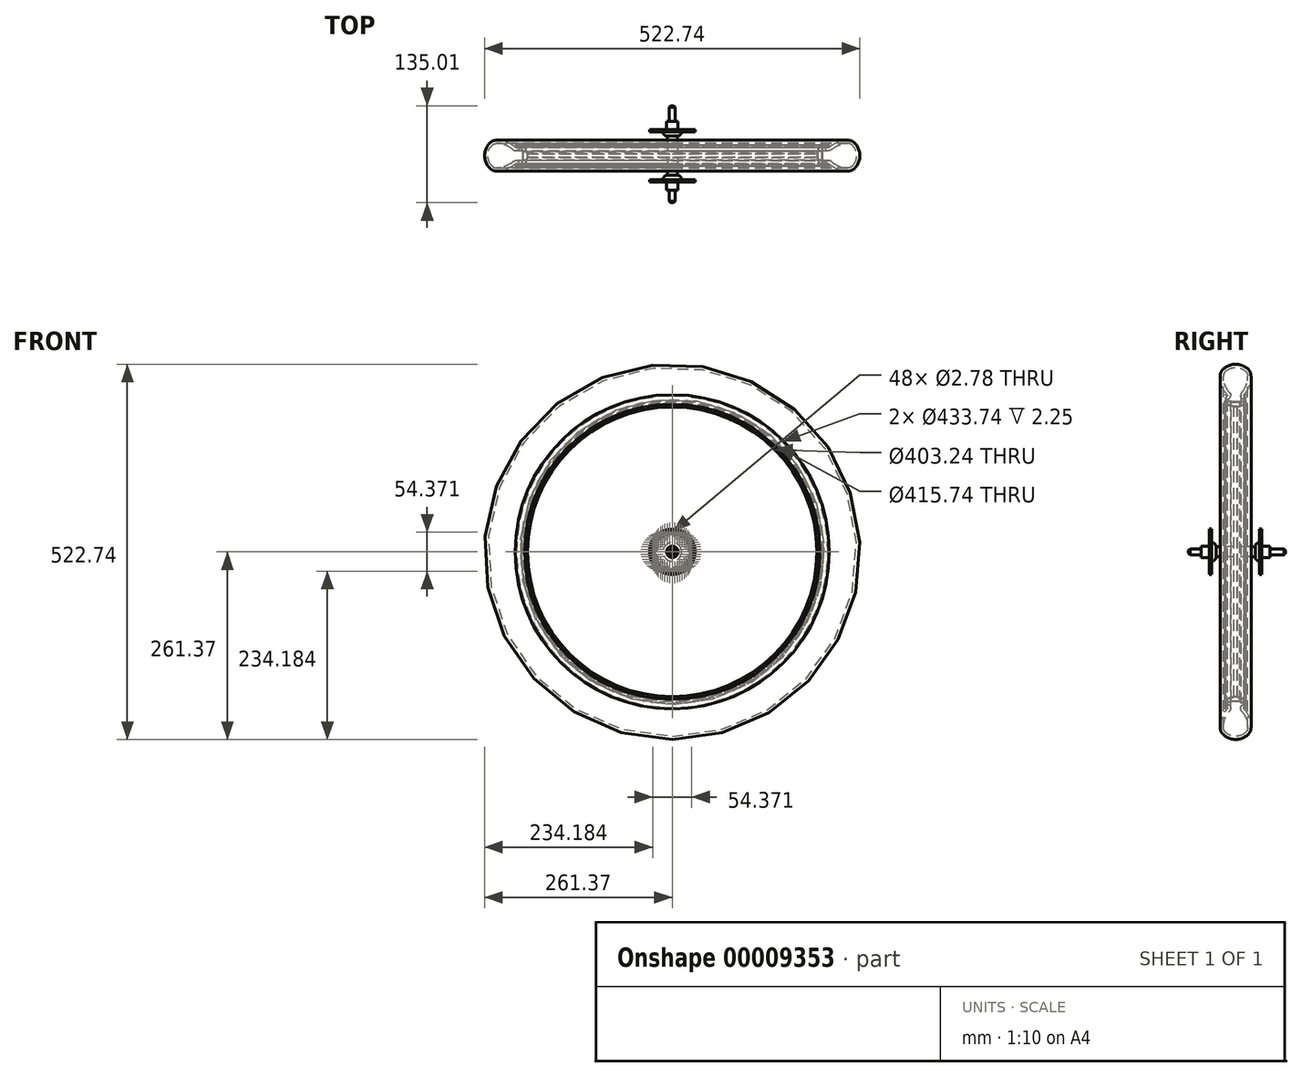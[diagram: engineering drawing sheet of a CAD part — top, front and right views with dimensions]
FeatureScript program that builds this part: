
annotation { "Feature Type Name" : "Feature", "Feature Type Description" : "" }
export const myFeature = defineFeature(function(context is Context, id is Id, definition is map)
    precondition{}
    {
        {
            var Q0;
            Q0=qCreatedBy(makeId("Front.planeOp"),FACE);
            var sketch = newSketch(context, id + "F0", { "sketchPlane" : qUnion([Q0])});
            skCircle(sketch, "E0", {"center": v(0, 0) * mm, "radius": 31.75 * mm});
            skCircle(sketch, "E1", {"center": v(0, 0) * mm, "radius": 4 * mm});
            skSolve(sketch);
        }
        {
            var Q0;
            Q0=qSketchRegion(id+"F0",true);
            extrude(context, id + "F1", {"entities" : qUnion([Q0]), "depth" : 3.17 * mm});
        }
        {
            var Q0;
            Q0=qCreatedBy(makeId("Right.planeOp"),FACE);
            var sketch = newSketch(context, id + "F2", { "sketchPlane" : qUnion([Q0])});
            skLineSegment(sketch, "E2", {"start": v(-31.75, 0) * mm, "end": v(31.75, 0) * mm, "construction": true});
            skLineSegment(sketch, "E3", {"start": v(-31.75, 27.19) * mm, "end": v(31.75, 27.19) * mm, "construction": true});
            skPoint(sketch, "E4", {"position": v(-3.18, 28.57) * mm});
            skLineSegment(sketch, "E5", {"start": v(-3.18, 31.75) * mm, "end": v(0, 31.75) * mm, "construction": true});
            skSolve(sketch);
        }
        {
            var Q0;
            Q0=qCreatedBy(makeId("Right.planeOp"),FACE);
            var sketch = newSketch(context, id + "F3", { "sketchPlane" : qUnion([Q0])});
            skLineSegment(sketch, "E6", {"start": v(-3.18, 27.19) * mm, "end": v(-3.18, 29.37) * mm});
            skLineSegment(sketch, "E7", {"start": v(-3.18, 29.37) * mm, "end": v(-2.7, 28.57) * mm});
            skLineSegment(sketch, "E8", {"start": v(-2.7, 28.57) * mm, "end": v(-0.48, 28.57) * mm});
            skLineSegment(sketch, "E9", {"start": v(-0.48, 28.57) * mm, "end": v(0, 29.37) * mm});
            skLineSegment(sketch, "E10", {"start": v(0, 29.37) * mm, "end": v(0, 27.19) * mm});
            skLineSegment(sketch, "E11", {"start": v(0, 27.19) * mm, "end": v(-3.18, 27.19) * mm});
            skLineSegment(sketch, "E12", {"start": v(-1.59, 27.19) * mm, "end": v(-1.59, 31.75) * mm, "construction": true});
            skSolve(sketch);
        }
        {
            var Q0;
            Q0=qSketchRegion(id+"F3",true);
            var Q1;
            Q1=sQuery(id+"F2.wireOp",EDGE,"E3");
            revolve(context, id + "F4", {"entities" : qUnion([Q0]), "axis" : qUnion([Q1]), "revolveType" : RevolveType.FULL, "oppositeDirection" : true});
        }
        {
            var Q0;
            Q0=makeQuery(id+"F4.opRevolve","SWEPT_BODY",BODY,{"disambiguationData":[OSD([sQuery(id+"F3.wireOp",EDGE,"E6"),sQuery(id+"F3.wireOp",EDGE,"E7"),sQuery(id+"F3.wireOp",EDGE,"E8"),sQuery(id+"F3.wireOp",EDGE,"E9"),sQuery(id+"F3.wireOp",EDGE,"E10"),sQuery(id+"F3.wireOp",EDGE,"E11")])]});
            var Q1;
            Q1=sQuery(id+"F2.wireOp",EDGE,"E2");
            circularPattern(context, id + "F5", {"operationType" : NewBodyOperationType.REMOVE, "entities" : qUnion([Q0]), "axis" : qUnion([Q1]), "angle" : 360 * degree, "instanceCount" : round(24), "equalSpace" : true});
        }
        {
            var Q0;
            Q0=makeQuery(id+"F1.opExtrude","SWEPT_BODY",BODY,{"disambiguationData":[OSD([sQuery(id+"F0.wireOp",EDGE,"E0"),sQuery(id+"F0.wireOp",EDGE,"E1")])]});
            var Q1;
            Q1=sQuery(id+"F2.wireOp",EDGE,"E2");
            transform(context, id + "F6", {"entities" : qUnion([Q0]), "transformType" : TransformType.TRANSLATION_DISTANCE, "transformDirection" : qUnion([Q1]), "distance" : 69.85 * mm, "makeCopy" : true});
        }
        {
            var Q0;
            Q0=makeQuery(id+"F6.opPattern","COPY",BODY,{"derivedFrom":makeQuery(id+"F1.opExtrude","SWEPT_BODY",BODY,{"disambiguationData":[OSD([sQuery(id+"F0.wireOp",EDGE,"E0"),sQuery(id+"F0.wireOp",EDGE,"E1")])]}),"instanceName":"1"});
            var Q1;
            Q1=sQuery(id+"F2.wireOp",EDGE,"E2");
            transform(context, id + "F7", {"entities" : qUnion([Q0]), "transformType" : TransformType.ROTATION, "transformAxis" : qUnion([Q1]), "angle" : 7.5 * degree, "makeCopy" : false});
        }
        {
            var Q0;
            Q0=qCreatedBy(makeId("Right.planeOp"),FACE);
            var sketch = newSketch(context, id + "F8", { "sketchPlane" : qUnion([Q0])});
            skLineSegment(sketch, "E13", {"start": v(0, 0) * mm, "end": v(66.68, 0) * mm, "construction": true});
            skLineSegment(sketch, "E14", {"start": v(33.34, 0) * mm, "end": v(33.34, 218.87) * mm, "construction": true});
            skSolve(sketch);
        }
        {
            var Q0;
            Q0=qCreatedBy(makeId("Front.planeOp"),FACE);
            var Q1;
            Q1=sQuery(id+"F8.wireOp",VERTEX,"E14.start");
            cPlane(context, id + "F9", {"entities" : qUnion([Q0, Q1]), "cplaneType" : CPlaneType.PLANE_POINT, "offset" : 150 * mm, "width" : 150 * mm, "height" : 150 * mm});
        }
        {
            var Q0;
            Q0=qCreatedBy(id+"F9.planeOp",FACE);
            var sketch = newSketch(context, id + "F10", { "sketchPlane" : qUnion([Q0])});
            skCircle(sketch, "E15", {"center": v(0, 0) * mm, "radius": 218.87 * mm, "construction": true});
            skSolve(sketch);
        }
        {
            var Q0;
            Q0=qCreatedBy(makeId("Right.planeOp"),FACE);
            var sketch = newSketch(context, id + "F11", { "sketchPlane" : qUnion([Q0])});
            skLineSegment(sketch, "E16", {"start": v(33.34, 201.62) * mm, "end": v(30.84, 201.62) * mm});
            skLineSegment(sketch, "E17", {"start": v(18.34, 218.87) * mm, "end": v(21.59, 218.87) * mm});
            skLineSegment(sketch, "E18", {"start": v(18.34, 218.87) * mm, "end": v(18.34, 205.53) * mm});
            skLineSegment(sketch, "E19", {"start": v(18.34, 205.53) * mm, "end": v(30.84, 201.62) * mm});
            skLineSegment(sketch, "E20", {"start": v(21.59, 218.87) * mm, "end": v(21.59, 216.87) * mm});
            skLineSegment(sketch, "E21", {"start": v(21.59, 216.87) * mm, "end": v(19.34, 216.87) * mm});
            skLineSegment(sketch, "E22", {"start": v(19.34, 216.87) * mm, "end": v(19.34, 211.37) * mm});
            skLineSegment(sketch, "E23", {"start": v(19.34, 211.37) * mm, "end": v(27.34, 208.87) * mm});
            skLineSegment(sketch, "E24", {"start": v(27.34, 208.87) * mm, "end": v(33.34, 208.87) * mm});
            skLineSegment(sketch, "E25", {"start": v(33.34, 207.87) * mm, "end": v(27.18, 207.87) * mm});
            skLineSegment(sketch, "E26", {"start": v(27.18, 207.87) * mm, "end": v(19.34, 210.32) * mm});
            skLineSegment(sketch, "E27", {"start": v(19.34, 210.32) * mm, "end": v(19.34, 206.26) * mm});
            skLineSegment(sketch, "E28", {"start": v(19.34, 206.26) * mm, "end": v(31, 202.62) * mm});
            skLineSegment(sketch, "E29", {"start": v(31, 202.62) * mm, "end": v(33.34, 202.62) * mm});
            skLineSegment(sketch, "E30", {"start": v(19.34, 214.12) * mm, "end": v(18.34, 214.12) * mm, "construction": true});
            skLineSegment(sketch, "E31", {"start": v(23.34, 210.12) * mm, "end": v(23.04, 209.17) * mm, "construction": true});
            skLineSegment(sketch, "E32", {"start": v(25.16, 204.44) * mm, "end": v(24.87, 203.49) * mm, "construction": true});
            skLineSegment(sketch, "E33", {"start": v(30.34, 208.87) * mm, "end": v(30.34, 207.87) * mm, "construction": true});
            skLineSegment(sketch, "E34", {"start": v(32.16, 202.62) * mm, "end": v(32.16, 201.62) * mm, "construction": true});
            skLineSegment(sketch, "E35", {"start": v(33.34, 218.87) * mm, "end": v(33.34, 208.87) * mm, "construction": true});
            skLineSegment(sketch, "E36.0.MirrorCS", {"start": v(39.34, 208.87) * mm, "end": v(33.34, 208.87) * mm});
            skLineSegment(sketch, "E37.0.MirrorCS", {"start": v(47.34, 211.37) * mm, "end": v(39.34, 208.87) * mm});
            skLineSegment(sketch, "E38.0.MirrorCS", {"start": v(47.34, 216.87) * mm, "end": v(47.34, 211.37) * mm});
            skLineSegment(sketch, "E39.0.MirrorCS", {"start": v(45.09, 216.87) * mm, "end": v(47.34, 216.87) * mm});
            skLineSegment(sketch, "E40.0.MirrorCS", {"start": v(45.09, 218.87) * mm, "end": v(45.09, 216.87) * mm});
            skLineSegment(sketch, "E41.0.MirrorCS", {"start": v(48.34, 218.87) * mm, "end": v(45.09, 218.87) * mm});
            skLineSegment(sketch, "E42.0.MirrorCS", {"start": v(48.34, 218.87) * mm, "end": v(48.34, 205.53) * mm});
            skLineSegment(sketch, "E43.0.MirrorCS", {"start": v(48.34, 205.53) * mm, "end": v(35.84, 201.62) * mm});
            skLineSegment(sketch, "E44.0.MirrorCS", {"start": v(33.34, 201.62) * mm, "end": v(35.84, 201.62) * mm});
            skLineSegment(sketch, "E45.0.MirrorCS", {"start": v(35.68, 202.62) * mm, "end": v(33.34, 202.62) * mm});
            skLineSegment(sketch, "E46.0.MirrorCS", {"start": v(47.34, 206.26) * mm, "end": v(35.68, 202.62) * mm});
            skLineSegment(sketch, "E47.0.MirrorCS", {"start": v(47.34, 210.32) * mm, "end": v(47.34, 206.26) * mm});
            skLineSegment(sketch, "E48.0.MirrorCS", {"start": v(39.5, 207.87) * mm, "end": v(47.34, 210.32) * mm});
            skLineSegment(sketch, "E49.0.MirrorCS", {"start": v(33.34, 207.87) * mm, "end": v(39.5, 207.87) * mm});
            skSolve(sketch);
        }
        {
            var Q0;
            Q0=qSketchRegion(id+"F11",true);
            var Q1;
            Q1=sQuery(id+"F8.wireOp",EDGE,"E13");
            revolve(context, id + "F12", {"entities" : qUnion([Q0]), "axis" : qUnion([Q1]), "revolveType" : RevolveType.FULL});
        }
        {
            var Q0;
            Q0=qCreatedBy(makeId("Right.planeOp"),FACE);
            var sketch = newSketch(context, id + "F13", { "sketchPlane" : qUnion([Q0])});
            skArc(sketch, "E50", {"start": v(21, 216.8) * mm, "mid": v(19.41, 214.05) * mm, "end": v(22.16, 212.46) * mm});
            skArc(sketch, "E51", {"start": v(21, 216.8) * mm, "mid": v(21.88, 217.64) * mm, "end": v(21.63, 218.83) * mm});
            skLineSegment(sketch, "E52", {"start": v(18.34, 261.37) * mm, "end": v(48.34, 261.37) * mm, "construction": true});
            skLineSegment(sketch, "E53", {"start": v(11.84, 261.37) * mm, "end": v(11.84, 218.87) * mm, "construction": true});
            skLineSegment(sketch, "E54", {"start": v(11.84, 244.87) * mm, "end": v(33.34, 244.87) * mm, "construction": true});
            skArc(sketch, "E55", {"start": v(11.84, 244.87) * mm, "mid": v(14.37, 230.96) * mm, "end": v(21.63, 218.83) * mm});
            skArc(sketch, "E56", {"start": v(33.34, 261.37) * mm, "mid": v(23.72, 259.45) * mm, "end": v(15.59, 253.98) * mm});
            skArc(sketch, "E57", {"start": v(15.59, 253.98) * mm, "mid": v(12.81, 249.8) * mm, "end": v(11.84, 244.87) * mm});
            skArc(sketch, "E58.0", {"start": v(22.16, 212.46) * mm, "mid": v(26.18, 216.33) * mm, "end": v(25, 221.79) * mm});
            skArc(sketch, "E58.1", {"start": v(16.33, 244.87) * mm, "mid": v(18.57, 232.54) * mm, "end": v(25, 221.79) * mm});
            skArc(sketch, "E58.2", {"start": v(18.77, 250.81) * mm, "mid": v(16.96, 248.09) * mm, "end": v(16.33, 244.87) * mm});
            skArc(sketch, "E58.3", {"start": v(33.34, 256.88) * mm, "mid": v(25.45, 255.3) * mm, "end": v(18.77, 250.81) * mm});
            skLineSegment(sketch, "E59", {"start": v(33.34, 261.37) * mm, "end": v(33.34, 218.87) * mm, "construction": true});
            skArc(sketch, "E60.0.MirrorCS", {"start": v(33.34, 261.37) * mm, "mid": v(42.95, 259.45) * mm, "end": v(51.09, 253.98) * mm});
            skArc(sketch, "E61.0.MirrorCS", {"start": v(51.09, 253.98) * mm, "mid": v(53.86, 249.8) * mm, "end": v(54.84, 244.87) * mm});
            skArc(sketch, "E62.0.MirrorCS", {"start": v(54.84, 244.87) * mm, "mid": v(52.3, 230.96) * mm, "end": v(45.05, 218.83) * mm});
            skArc(sketch, "E63.0.MirrorCS", {"start": v(45.67, 216.8) * mm, "mid": v(44.8, 217.64) * mm, "end": v(45.05, 218.83) * mm});
            skArc(sketch, "E64.0.MirrorCS", {"start": v(45.67, 216.8) * mm, "mid": v(47.26, 214.05) * mm, "end": v(44.52, 212.46) * mm});
            skArc(sketch, "E65.0.MirrorCS", {"start": v(44.52, 212.46) * mm, "mid": v(40.5, 216.33) * mm, "end": v(41.67, 221.79) * mm});
            skArc(sketch, "E66.0.MirrorCS", {"start": v(50.35, 244.87) * mm, "mid": v(48.1, 232.54) * mm, "end": v(41.67, 221.79) * mm});
            skArc(sketch, "E67.0.MirrorCS", {"start": v(47.9, 250.81) * mm, "mid": v(49.71, 248.09) * mm, "end": v(50.35, 244.87) * mm});
            skArc(sketch, "E68.0.MirrorCS", {"start": v(33.34, 256.88) * mm, "mid": v(41.23, 255.3) * mm, "end": v(47.9, 250.81) * mm});
            skSolve(sketch);
        }
        {
            var Q0;
            Q0=qSketchRegion(id+"F13",true);
            var Q1;
            Q1=sQuery(id+"F8.wireOp",EDGE,"E13");
            revolve(context, id + "F14", {"entities" : qUnion([Q0]), "axis" : qUnion([Q1]), "revolveType" : RevolveType.FULL});
        }
        {
            var Q0;
            Q0=qCreatedBy(makeId("Right.planeOp"),FACE);
            var sketch = newSketch(context, id + "F15", { "sketchPlane" : qUnion([Q0])});
            skLineSegment(sketch, "E69", {"start": v(0, 13) * mm, "end": v(0, 7) * mm});
            skLineSegment(sketch, "E70", {"start": v(0, 4) * mm, "end": v(33.34, 4) * mm});
            skLineSegment(sketch, "E71", {"start": v(6, 7) * mm, "end": v(33.34, 7) * mm});
            skLineSegment(sketch, "E72", {"start": v(6, 7) * mm, "end": v(0, 7) * mm, "construction": true});
            skArc(sketch, "E73", {"start": v(6, 7) * mm, "mid": v(4.24, 11.24) * mm, "end": v(0, 13) * mm});
            skLineSegment(sketch, "E74", {"start": v(0, 7) * mm, "end": v(0, 4) * mm});
            skLineSegment(sketch, "E75.0.MirrorCS", {"start": v(60.68, 7) * mm, "end": v(33.34, 7) * mm});
            skArc(sketch, "E76.0.MirrorCS", {"start": v(60.68, 7) * mm, "mid": v(62.43, 11.24) * mm, "end": v(66.68, 13) * mm});
            skLineSegment(sketch, "E77.0.MirrorCS", {"start": v(66.68, 13) * mm, "end": v(66.68, 7) * mm});
            skLineSegment(sketch, "E78.0.MirrorCS", {"start": v(66.68, 7) * mm, "end": v(66.68, 4) * mm});
            skLineSegment(sketch, "E79.0.MirrorCS", {"start": v(66.68, 4) * mm, "end": v(33.34, 4) * mm});
            skSolve(sketch);
        }
        {
            var Q0;
            Q0 = qSketchRegion(id + "F15", true);
            var Q1;
            Q1=sQuery(id+"F8.wireOp",EDGE,"E13");
            revolve(context, id + "F16", {"operationType" : NewBodyOperationType.ADD, "entities" : qUnion([Q0]), "axis" : qUnion([Q1]), "revolveType" : RevolveType.FULL});
        }
        {
            var Q0;
            Q0=makeQuery(id+"F1.opExtrude","CAP_FACE",FACE,{"disambiguationData":[OSD([sQuery(id+"F0.wireOp",EDGE,"E0"),sQuery(id+"F0.wireOp",EDGE,"E1")])],"isStart":false});
            var sketch = newSketch(context, id + "F17", { "sketchPlane" : qUnion([Q0])});
            skCircle(sketch, "E80", {"center": v(0, 0) * mm, "radius": 4 * mm});
            skSolve(sketch);
        }
        {
            var Q0;
            Q0 = qSketchRegion(id + "F17", true);
            extrude(context, id + "F18", {"entities" : qUnion([Q0]), "depth" : 29 * mm, "hasSecondDirection" : true, "secondDirectionOppositeDirection" : true, "secondDirectionDepth" : 106 * mm});
        }
        {
            var Q0;
            Q0=makeQuery(id+"F18.opExtrude","CAP_EDGE",EDGE,{"disambiguationData":[OSD([sQuery(id+"F17.wireOp",EDGE,"E80")])],"isStart":false});
            var Q1;
            Q1=makeQuery(id+"F18.opExtrude","CAP_EDGE",EDGE,{"disambiguationData":[OSD([sQuery(id+"F17.wireOp",EDGE,"E80")])],"isStart":true});
            chamfer(context, id + "F19", {"entities" : qUnion([Q0, Q1]), "width" : 2 * mm, "tangentPropagation" : true});
        }
        {
            var Q0;
            Q0=qCreatedBy(id+"F9.planeOp",FACE);
            cPlane(context, id + "F20", {"entities" : qUnion([Q0]), "cplaneType" : CPlaneType.OFFSET, "offset" : 48 * mm, "width" : 150 * mm, "height" : 150 * mm});
        }
        {
            var Q0;
            Q0=makeQuery(id+"F1.opExtrude","CAP_FACE",FACE,{"disambiguationData":[OSD([sQuery(id+"F0.wireOp",EDGE,"E0"),sQuery(id+"F0.wireOp",EDGE,"E1")])],"isStart":false});
            var sketch = newSketch(context, id + "F21", { "sketchPlane" : qUnion([Q0])});
            skCircle(sketch, "E81", {"center": v(0, 0) * mm, "radius": 4 * mm});
            skCircle(sketch, "E82", {"center": v(0, 0) * mm, "radius": 8 * mm});
            skSolve(sketch);
        }
        {
            var Q0;
            Q0 = qSketchRegion(id + "F21", true);
            var Q1;
            Q1=qCreatedBy(id+"F20.planeOp",FACE);
            extrude(context, id + "F22", {"entities" : qUnion([Q0]), "endBound" : BoundingType.UP_TO_SURFACE, "endBoundEntityFace" : qUnion([Q1]), "depth" : 25 * mm});
        }
        {
            var Q0;
            Q0=makeQuery(id+"F22.opExtrude","SWEPT_BODY",BODY,{"disambiguationData":[OSD([sQuery(id+"F21.wireOp",EDGE,"E81"),sQuery(id+"F21.wireOp",EDGE,"E82")])]});
            var Q1;
            Q1=qCreatedBy(id+"F9.planeOp",FACE);
            mirror(context, id + "F23", {"operationType" : NewBodyOperationType.ADD, "entities" : qUnion([Q0]), "mirrorPlane" : qUnion([Q1])});
        }
    });
